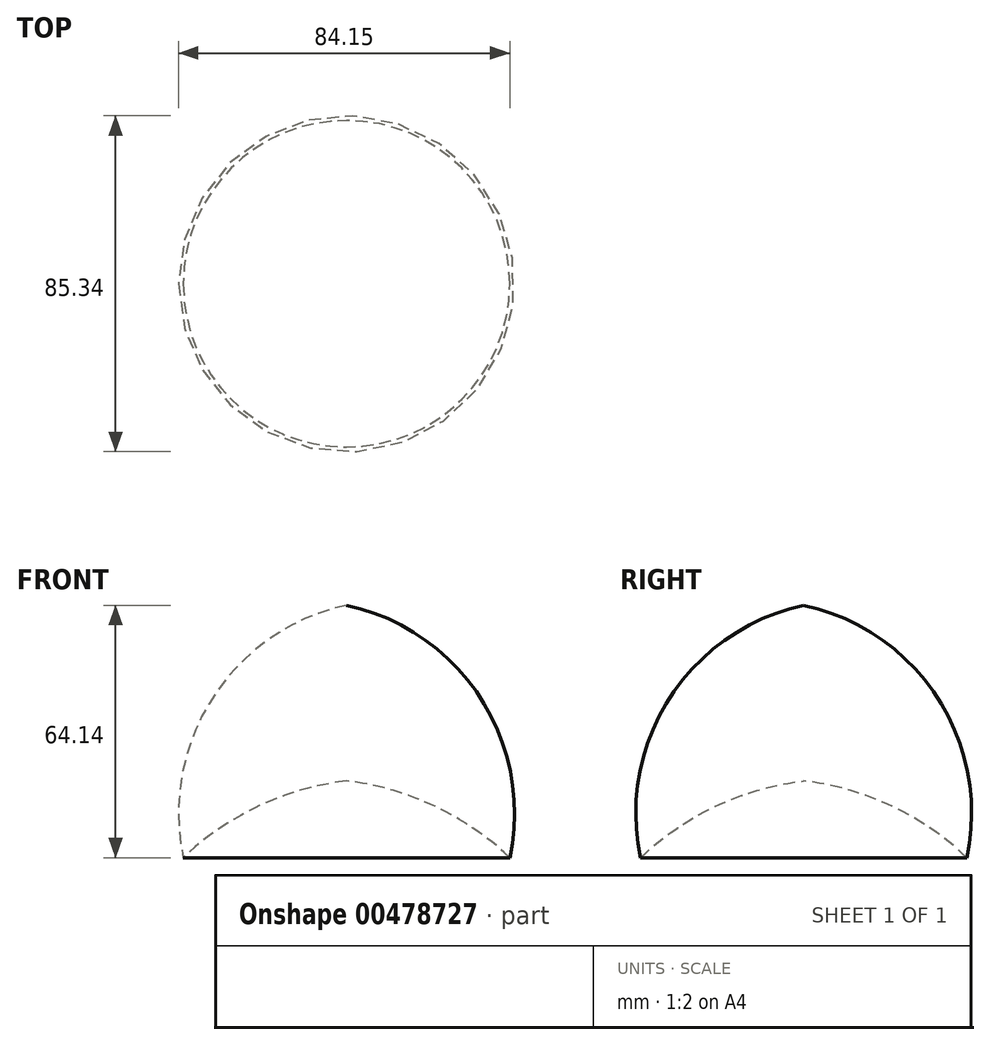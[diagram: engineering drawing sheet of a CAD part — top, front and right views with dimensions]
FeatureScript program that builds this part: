
annotation { "Feature Type Name" : "Feature", "Feature Type Description" : "" }
export const myFeature = defineFeature(function(context is Context, id is Id, definition is map)
    precondition{}
    {
        {
            var Q0;
            Q0=qCreatedBy(makeId("Front.planeOp"),FACE);
            var sketch = newSketch(context, id + "F0", { "sketchPlane" : qUnion([Q0])});
            skArc(sketch, "E0", {"start": v(41.48, 0) * mm, "mid": v(34, 40.65) * mm, "end": v(0, 64.14) * mm});
            skArc(sketch, "E1", {"start": v(41.48, 0) * mm, "mid": v(22.32, 13.11) * mm, "end": v(0, 19.5) * mm});
            skLineSegment(sketch, "E2", {"start": v(0, 64.14) * mm, "end": v(0, 19.5) * mm});
            skSolve(sketch);
        }
        {
            var Q0;
            Q0=makeQuery(id+"F0.imprint","IMPRINT",FACE,{"disambiguationData":[TD([[makeQuery(id+"F0.imprint","IMPRINT",EDGE,{"derivedFrom":sQuery(id+"F0.wireOp",EDGE,"E0")}),1.0]])]});
            var Q1;
            Q1=sQuery(id+"F0.wireOp",EDGE,"E2");
            revolve(context, id + "F1", {"entities" : qUnion([Q0]), "axis" : qUnion([Q1]), "revolveType" : RevolveType.FULL});
        }
    });
